# Revit family: Shower Valve-Brizo-Litze_Collection-Bath-Lever Handle
name_source: partatom
category: Plumbing Fixtures
units: mm (PartAtom-declared; Revit-internal decimal feet)

## family parameters
Always vertical = Yes
Cut with Voids When Loaded = No
OmniClass Number = 23.45.00.00
OmniClass Title = Sanitary, Laundry, and Cleaning Equipment
Part Type = Normal
Room Calculation Point = No
Round Connector Dimension = Use Radius
Shared = No
Work Plane-Based = Yes

## types (1)
- Brillance® Lux Gold™
    Actual Valve Water Flow = 0
    Assembly Code = D2010400
    Connector Radius = 0' - 0 1/2"
    Default Elevation = 4' - 0"
    Description = TempAssure Thermostatic Valve and Shower
    Design Valve Water Flow = 0
    Diameter = 0' - 6 1/2"
    Finish = Gold-Brizo-Brilliance® Luxe Gold™
    Flow = 0 GPM
    Makeup Water Flow = 0
    Manufacturer = Brizo
    Model = T60035 & T60235
    Product Documentation Link = http://brizopresskit.com
    Product Name = Litze™ Collection
    Shower Offset = 2' - 2 15/32"
    Style = Tub and Shower Valve
    Type Comments = Brillance® Lux Gold™
    URL = http://www.brizo.com
    Vent Connection = No
    Waste Connection = No

## geometry (parser evidence)
native form markers: Blend x6, Sweep x8
no freeform markers — native parametric forms only
